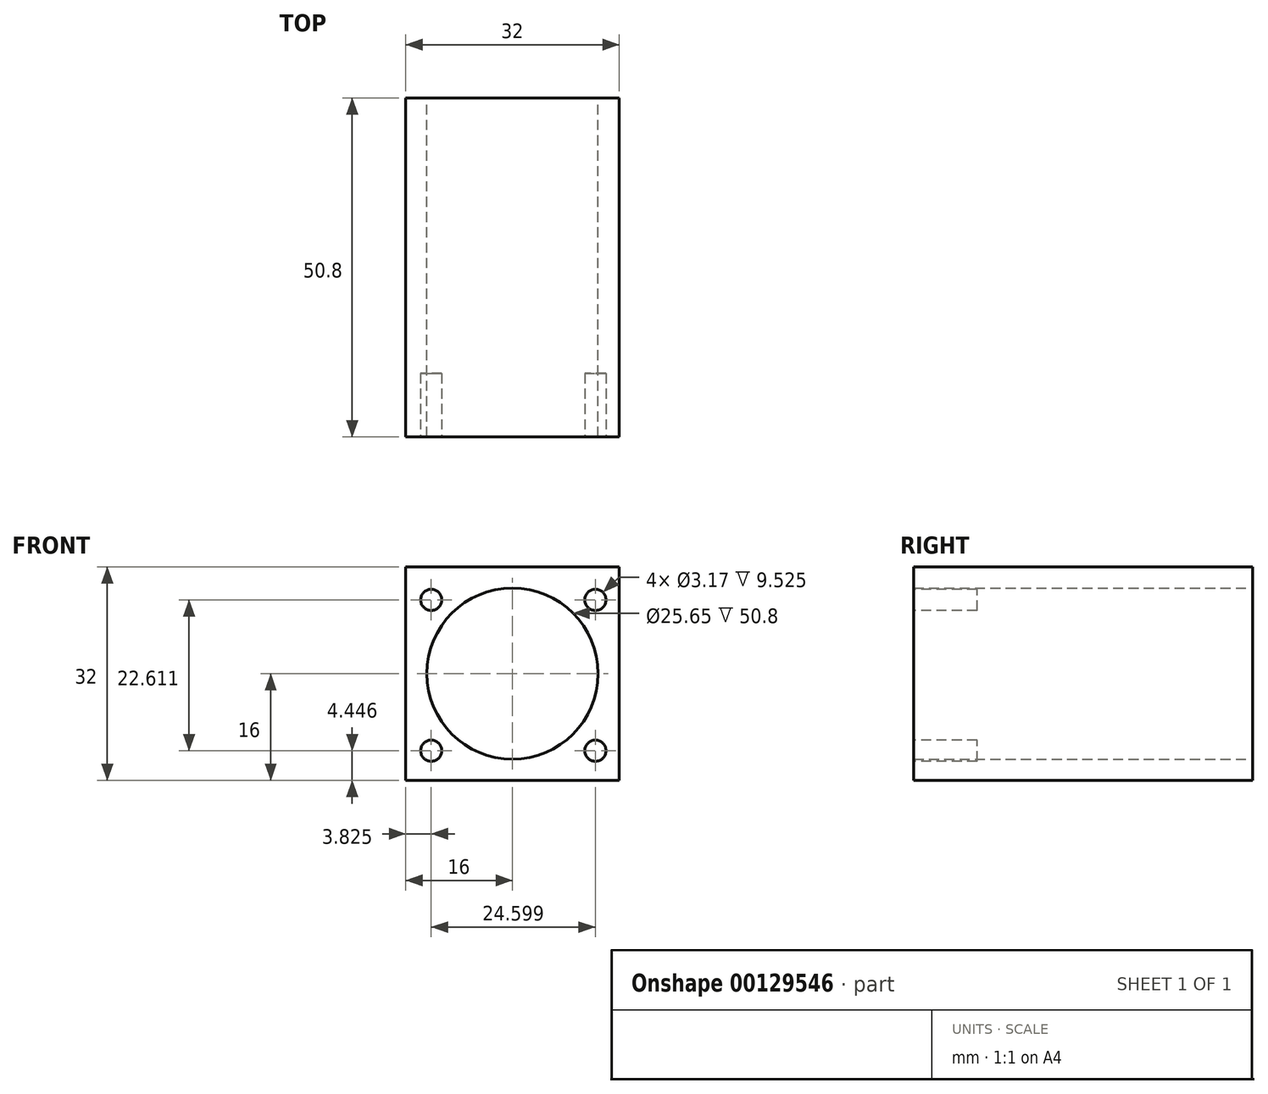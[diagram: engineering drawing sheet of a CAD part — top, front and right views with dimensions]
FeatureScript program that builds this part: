
annotation { "Feature Type Name" : "Feature", "Feature Type Description" : "" }
export const myFeature = defineFeature(function(context is Context, id is Id, definition is map)
    precondition{}
    {
        {
            var Q0;
            Q0=qCreatedBy(makeId("Front.planeOp"),FACE);
            var sketch = newSketch(context, id + "F0", { "sketchPlane" : qUnion([Q0])});
            skCircle(sketch, "E0", {"center": v(0, 0) * mm, "radius": 12.83 * mm});
            skLineSegment(sketch, "E1.bottom", {"start": v(16, -16) * mm, "end": v(-16, -16) * mm});
            skLineSegment(sketch, "E1.top", {"start": v(16, 16) * mm, "end": v(-16, 16) * mm});
            skLineSegment(sketch, "E1.left", {"start": v(16, -16) * mm, "end": v(16, 16) * mm});
            skLineSegment(sketch, "E1.right", {"start": v(-16, -16) * mm, "end": v(-16, 16) * mm});
            skSolve(sketch);
        }
        {
            var Q0;
            Q0 = qSketchRegion(id + "F0", true);
            extrude(context, id + "F1", {"entities" : qUnion([Q0]), "depth" : 50.8 * mm});
        }
        {
            var Q0;
            Q0=makeQuery(id+"F1.opExtrude","CAP_FACE",FACE,{"disambiguationData":[OSD([sQuery(id+"F0.wireOp",EDGE,"E0"),sQuery(id+"F0.wireOp",EDGE,"E1.bottom"),sQuery(id+"F0.wireOp",EDGE,"E1.top"),sQuery(id+"F0.wireOp",EDGE,"E1.left"),sQuery(id+"F0.wireOp",EDGE,"E1.right")])],"isStart":false});
            var sketch = newSketch(context, id + "F2", { "sketchPlane" : qUnion([Q0])});
            skCircle(sketch, "E2", {"center": v(-12.18, 11.06) * mm, "radius": 1.59 * mm});
            skCircle(sketch, "E3", {"center": v(12.42, 11.06) * mm, "radius": 1.59 * mm});
            skCircle(sketch, "E4", {"center": v(12.42, -11.55) * mm, "radius": 1.59 * mm});
            skCircle(sketch, "E5", {"center": v(-12.18, -11.55) * mm, "radius": 1.59 * mm});
            skSolve(sketch);
        }
        {
            var Q0;
            Q0 = qSketchRegion(id + "F2", true);
            extrude(context, id + "F3", {"entities" : qUnion([Q0]), "operationType" : NewBodyOperationType.REMOVE, "oppositeDirection" : true, "depth" : 9.52 * mm});
        }
    });
